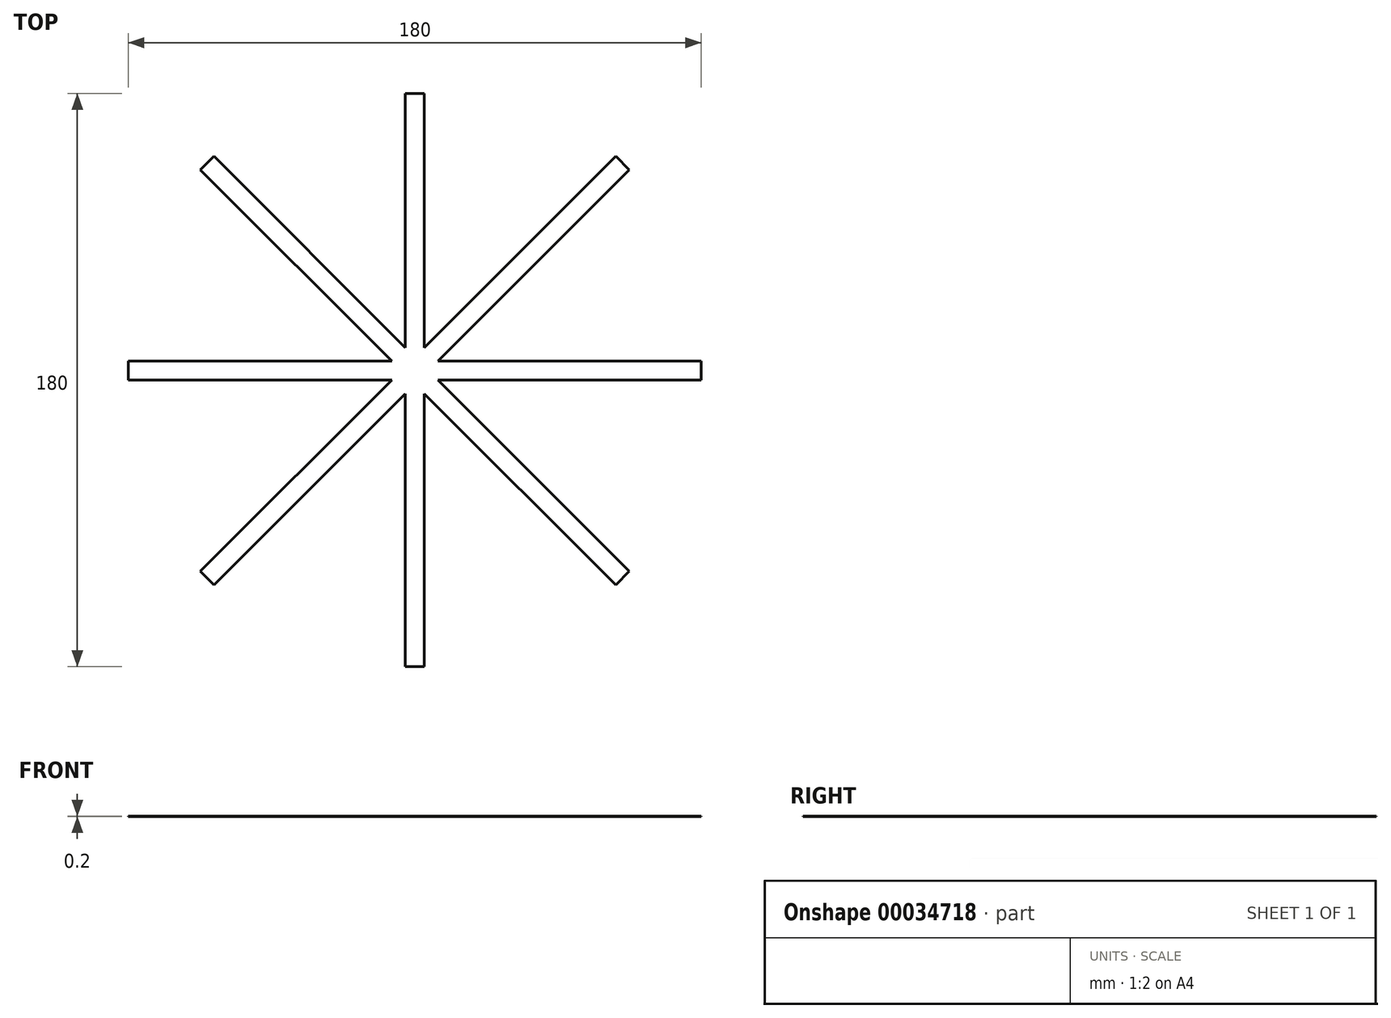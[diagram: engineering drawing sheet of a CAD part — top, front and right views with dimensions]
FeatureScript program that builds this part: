
annotation { "Feature Type Name" : "Feature", "Feature Type Description" : "" }
export const myFeature = defineFeature(function(context is Context, id is Id, definition is map)
    precondition{}
    {
        {
            var Q0;
            Q0=qCreatedBy(makeId("Top.planeOp"),FACE);
            var sketch = newSketch(context, id + "F0", { "sketchPlane" : qUnion([Q0])});
            skLineSegment(sketch, "E0.bottom", {"start": v(-3, 87.02) * mm, "end": v(3, 87.02) * mm});
            skLineSegment(sketch, "E0.top", {"start": v(-3, -92.98) * mm, "end": v(3, -92.98) * mm});
            skLineSegment(sketch, "E0.left", {"start": v(-3, 87.02) * mm, "end": v(-3, -92.98) * mm});
            skLineSegment(sketch, "E0.right", {"start": v(3, 87.02) * mm, "end": v(3, -92.98) * mm});
            skLineSegment(sketch, "E1.bottom", {"start": v(90, 3) * mm, "end": v(-90, 3) * mm});
            skLineSegment(sketch, "E1.top", {"start": v(90, -3) * mm, "end": v(-90, -3) * mm});
            skLineSegment(sketch, "E1.left", {"start": v(90, 3) * mm, "end": v(90, -3) * mm});
            skLineSegment(sketch, "E1.right", {"start": v(-90, 3) * mm, "end": v(-90, -3) * mm});
            skPoint(sketch, "E1.middle", {"position": v(0, 0) * mm});
            skLineSegment(sketch, "E2", {"start": v(-3, 7.24) * mm, "end": v(-63.1, 67.35) * mm});
            skLineSegment(sketch, "E3", {"start": v(-7.24, 3) * mm, "end": v(-67.35, 63.1) * mm});
            skLineSegment(sketch, "E4", {"start": v(-67.35, 63.1) * mm, "end": v(-63.1, 67.35) * mm});
            skLineSegment(sketch, "E5", {"start": v(-7.24, 3) * mm, "end": v(-3, 7.24) * mm});
            skLineSegment(sketch, "E6", {"start": v(0, 0) * mm, "end": v(-14.06, -14.06) * mm, "construction": true});
            skCircle(sketch, "E7", {"center": v(0, 0) * mm, "radius": 100 * mm, "construction": true});
            skLineSegment(sketch, "E8", {"start": v(0, 0) * mm, "end": v(-3, 0) * mm});
            skLineSegment(sketch, "E9", {"start": v(0, 0) * mm, "end": v(3, 0) * mm});
            skLineSegment(sketch, "E10.MirrorCS", {"start": v(3, -7.24) * mm, "end": v(7.24, -3) * mm});
            skLineSegment(sketch, "E11.MirrorCS", {"start": v(7.24, -3) * mm, "end": v(67.35, -63.1) * mm});
            skLineSegment(sketch, "E12.MirrorCS", {"start": v(3, -7.24) * mm, "end": v(63.1, -67.35) * mm});
            skLineSegment(sketch, "E13.MirrorCS", {"start": v(63.1, -67.35) * mm, "end": v(67.35, -63.1) * mm});
            skLineSegment(sketch, "E14.MirrorCS", {"start": v(3, 7.24) * mm, "end": v(63.1, 67.35) * mm});
            skLineSegment(sketch, "E15.MirrorCS", {"start": v(7.24, 3) * mm, "end": v(67.35, 63.1) * mm});
            skLineSegment(sketch, "E16.MirrorCS", {"start": v(7.24, 3) * mm, "end": v(3, 7.24) * mm});
            skLineSegment(sketch, "E17.MirrorCS", {"start": v(67.35, 63.1) * mm, "end": v(63.1, 67.35) * mm});
            skLineSegment(sketch, "E18.MirrorCS", {"start": v(-7.24, -3) * mm, "end": v(-67.35, -63.1) * mm});
            skLineSegment(sketch, "E19.MirrorCS", {"start": v(-3, -7.24) * mm, "end": v(-63.1, -67.35) * mm});
            skLineSegment(sketch, "E20.MirrorCS", {"start": v(-3, -7.24) * mm, "end": v(-7.24, -3) * mm});
            skLineSegment(sketch, "E21.MirrorCS", {"start": v(-63.1, -67.35) * mm, "end": v(-67.35, -63.1) * mm});
            skSolve(sketch);
        }
        {
            var Q0;
            Q0 = qSketchRegion(id + "F0", true);
            var Q1;
            {var subQ0=sQuery(id+"F0.wireOp",EDGE,"fgMRhXcz-fXm6-iqGZ-nvqP-u1NJdhZLuvN9");var subQ1=sQuery(id+"F0.wireOp",EDGE,"E0.left");var subQ2=makeQuery(id+"F0.imprint","INTERSECT",VERTEX,{"disambiguationData":[OD(1.0)],"derivedFrom":[subQ1,subQ0]});Q1=makeQuery(id+"F0.imprint","IMPRINT",FACE,{"disambiguationData":[TD([[makeQuery(id+"F0.imprint","IMPRINT",EDGE,{"disambiguationData":[TD([[subQ2,-1.0]])],"derivedFrom":subQ1}),-1.0]])]});}
            var Q2;
            {var subQ0=sQuery(id+"F0.wireOp",EDGE,"E1.bottom");var subQ1=sQuery(id+"F0.wireOp",EDGE,"E0.left");var subQ2=makeQuery(id+"F0.imprint","INTERSECT",VERTEX,{"derivedFrom":[subQ1,subQ0]});Q2=makeQuery(id+"F0.imprint","IMPRINT",FACE,{"disambiguationData":[TD([[makeQuery(id+"F0.imprint","IMPRINT",EDGE,{"disambiguationData":[TD([[subQ2,-1.0]])],"derivedFrom":subQ1}),1.0]])]});}
            var Q3;
            {var subQ0=sQuery(id+"F0.wireOp",EDGE,"fgMRhXcz-fXm6-iqGZ-nvqP-u1NJdhZLuvN9");var subQ8=sQuery(id+"F0.wireOp",EDGE,"E0.left");var subQ9=makeQuery(id+"F0.imprint","INTERSECT",VERTEX,{"disambiguationData":[OD(1.0)],"derivedFrom":[subQ8,subQ0]});Q3=makeQuery(id+"F0.imprint","IMPRINT",FACE,{"disambiguationData":[TD([[makeQuery(id+"F0.imprint","IMPRINT",EDGE,{"disambiguationData":[TD([[subQ9,-1.0]])],"derivedFrom":subQ8}),1.0]])]});}
            var Q4;
            {var subQ0=sQuery(id+"F0.wireOp",EDGE,"82H1LetX-IO8O-Rl4a-ccHY-xfmtxEjhRpvp");var subQ1=sQuery(id+"F0.wireOp",EDGE,"E1.bottom");var subQ2=makeQuery(id+"F0.imprint","INTERSECT",VERTEX,{"disambiguationData":[OD(1.0)],"derivedFrom":[subQ1,subQ0]});Q4=makeQuery(id+"F0.imprint","IMPRINT",FACE,{"disambiguationData":[TD([[makeQuery(id+"F0.imprint","IMPRINT",EDGE,{"disambiguationData":[TD([[subQ2,-1.0]])],"derivedFrom":subQ1}),-1.0]])]});}
            var Q5;
            {var subQ0=sQuery(id+"F0.wireOp",EDGE,"82H1LetX-IO8O-Rl4a-ccHY-xfmtxEjhRpvp");var subQ1=sQuery(id+"F0.wireOp",EDGE,"E0.left");var subQ2=makeQuery(id+"F0.imprint","INTERSECT",VERTEX,{"disambiguationData":[OD(1.0)],"derivedFrom":[subQ1,subQ0]});Q5=makeQuery(id+"F0.imprint","IMPRINT",FACE,{"disambiguationData":[TD([[makeQuery(id+"F0.imprint","IMPRINT",EDGE,{"disambiguationData":[TD([[subQ2,-1.0]])],"derivedFrom":subQ1}),1.0]])]});}
            var Q6;
            {var subQ0=sQuery(id+"F0.wireOp",EDGE,"fgMRhXcz-fXm6-iqGZ-nvqP-u1NJdhZLuvN9");var subQ1=sQuery(id+"F0.wireOp",EDGE,"E1.top");var subQ2=makeQuery(id+"F0.imprint","INTERSECT",VERTEX,{"disambiguationData":[OD(1.0)],"derivedFrom":[subQ1,subQ0]});Q6=makeQuery(id+"F0.imprint","IMPRINT",FACE,{"disambiguationData":[TD([[makeQuery(id+"F0.imprint","IMPRINT",EDGE,{"disambiguationData":[TD([[subQ2,-1.0]])],"derivedFrom":subQ1}),1.0]])]});}
            var Q7;
            {var subQ0=sQuery(id+"F0.wireOp",EDGE,"fgMRhXcz-fXm6-iqGZ-nvqP-u1NJdhZLuvN9");var subQ1=sQuery(id+"F0.wireOp",EDGE,"E0.right");var subQ2=makeQuery(id+"F0.imprint","INTERSECT",VERTEX,{"disambiguationData":[OD(1.0)],"derivedFrom":[subQ1,subQ0]});Q7=makeQuery(id+"F0.imprint","IMPRINT",FACE,{"disambiguationData":[TD([[makeQuery(id+"F0.imprint","IMPRINT",EDGE,{"disambiguationData":[TD([[subQ2,-1.0]])],"derivedFrom":subQ1}),-1.0]])]});}
            var Q8;
            {var subQ0=sQuery(id+"F0.wireOp",EDGE,"82H1LetX-IO8O-Rl4a-ccHY-xfmtxEjhRpvp");var subQ1=sQuery(id+"F0.wireOp",EDGE,"E0.right");var subQ2=makeQuery(id+"F0.imprint","INTERSECT",VERTEX,{"disambiguationData":[OD(1.0)],"derivedFrom":[subQ1,subQ0]});Q8=makeQuery(id+"F0.imprint","IMPRINT",FACE,{"disambiguationData":[TD([[makeQuery(id+"F0.imprint","IMPRINT",EDGE,{"disambiguationData":[TD([[subQ2,-1.0]])],"derivedFrom":subQ1}),1.0]])]});}
            var Q9;
            {var subQ0=sQuery(id+"F0.wireOp",EDGE,"E1.bottom");var subQ1=sQuery(id+"F0.wireOp",EDGE,"E0.right");var subQ2=makeQuery(id+"F0.imprint","INTERSECT",VERTEX,{"derivedFrom":[subQ1,subQ0]});Q9=makeQuery(id+"F0.imprint","IMPRINT",FACE,{"disambiguationData":[TD([[makeQuery(id+"F0.imprint","IMPRINT",EDGE,{"disambiguationData":[TD([[subQ2,-1.0]])],"derivedFrom":subQ1}),-1.0]])]});}
            extrude(context, id + "F1", {"entities" : qUnion([Q0, Q1, Q2, Q3, Q4, Q5, Q6, Q7, Q8, Q9]), "depth" : 0.2 * mm});
        }
    });
